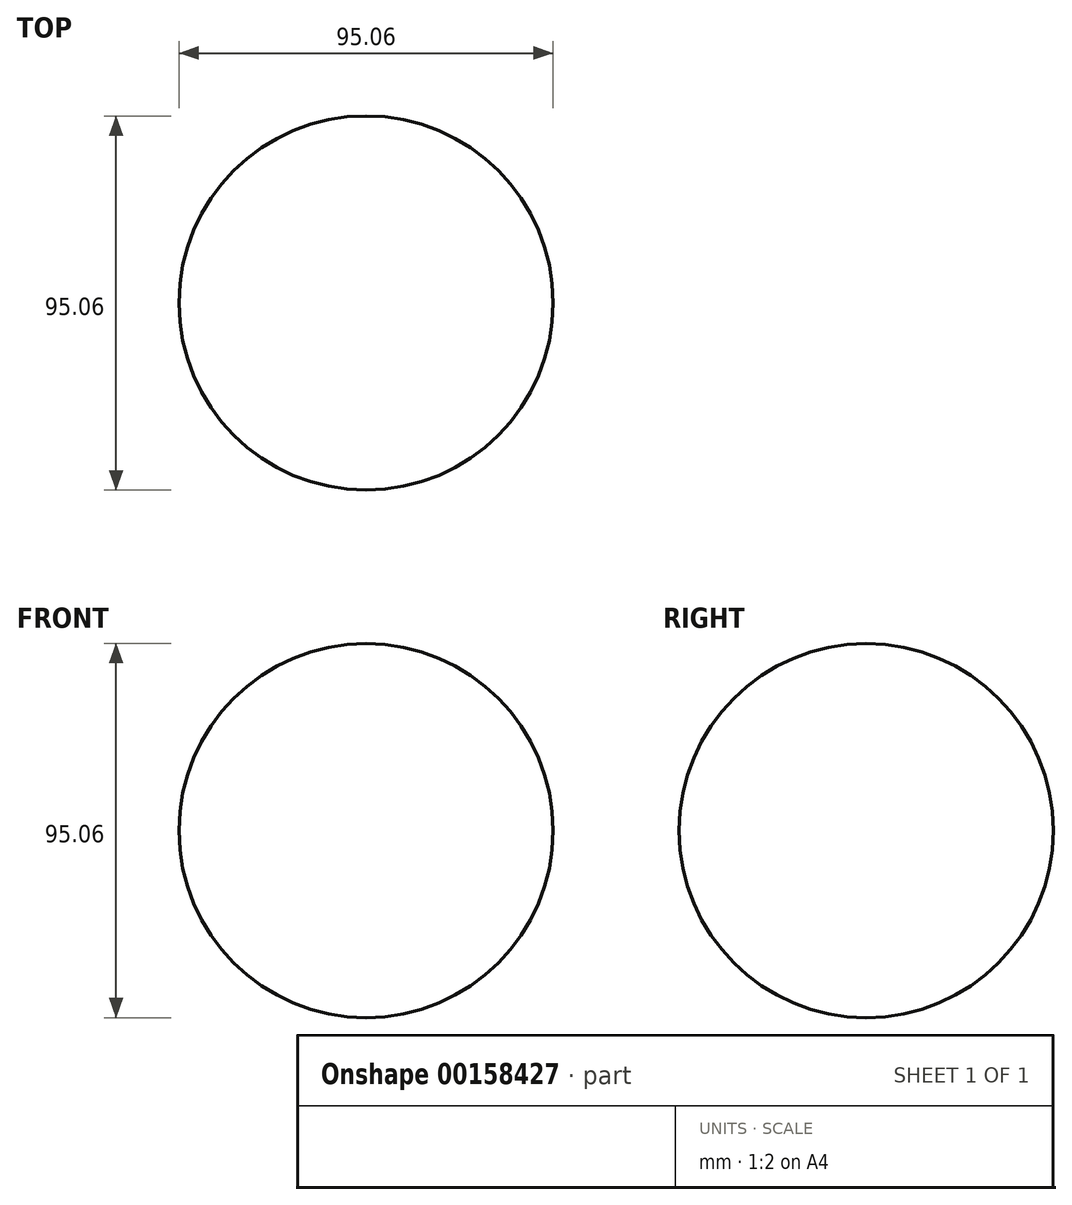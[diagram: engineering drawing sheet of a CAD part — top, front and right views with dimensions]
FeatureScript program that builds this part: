
annotation { "Feature Type Name" : "Feature", "Feature Type Description" : "" }
export const myFeature = defineFeature(function(context is Context, id is Id, definition is map)
    precondition{}
    {
        {
            var Q0;
            Q0=qCreatedBy(makeId("Top.planeOp"),FACE);
            var sketch = newSketch(context, id + "F0", { "sketchPlane" : qUnion([Q0])});
            skArc(sketch, "E0", {"start": v(0, -47.53) * mm, "mid": v(47.53, 0) * mm, "end": v(0, 47.53) * mm});
            skLineSegment(sketch, "E1", {"start": v(0, 47.53) * mm, "end": v(0, -47.53) * mm});
            skSolve(sketch);
        }
        {
            var Q0;
            Q0=makeQuery(id+"F0.imprint","IMPRINT",FACE,{"disambiguationData":[TD([[makeQuery(id+"F0.imprint","IMPRINT",EDGE,{"derivedFrom":sQuery(id+"F0.wireOp",EDGE,"E0")}),1.0]])]});
            var Q1;
            Q1=sQuery(id+"F0.wireOp",EDGE,"E1");
            revolve(context, id + "F1", {"entities" : qUnion([Q0]), "axis" : qUnion([Q1]), "revolveType" : RevolveType.FULL});
        }
    });
